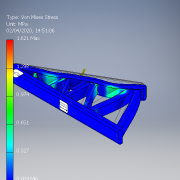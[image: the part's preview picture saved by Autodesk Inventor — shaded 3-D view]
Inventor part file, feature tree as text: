
AUTODESK INVENTOR PART (.ipt)
format: ipt  version: 2018.3 (Build 223284000, 284)  size: 271,872 bytes
history: native  units: mm
features: fillet x3, extrude x2, sketch x2, plane x1
ambient origin geometry x8: Origin, YZ Plane, XZ Plane, XY Plane, X Axis, Y Axis, Z Axis, Center Point
bodies: Solid1 (feature_tree)
feature tree (8):
  extrude  "Extrusion1"  Depth=6.0mm
  fillet  "Fillet1"  Radius=6.0mm
  fillet  "Fillet2"  Radius=15.0mm
  fillet  "Fillet3"  Radius=2.0mm
  plane  "Work Plane1"
  extrude  "Extrusion5"  Depth=2.0mm
  sketch  "Sketch1"  dims[d0=130.0mm d1=6.0mm d2=6.0mm d3=15.0mm d4=0.0mm d5=2.0mm]
  sketch  "Sketch2"  dims[d6=2.0mm d7=2.0mm d8=120.0deg d9=15.0mm d10=30.0deg d15=1.5mm d18=90.0deg d28=3.0mm d29=60.0deg d30=3.0mm d31=90.0deg d32=4.0mm d47=30.0deg d51=60.0deg d52=6.0mm d54=6.0mm d55=4.0mm d56=60.0deg d57=115.0mm d58=10.0mm d59=0.0mm]
